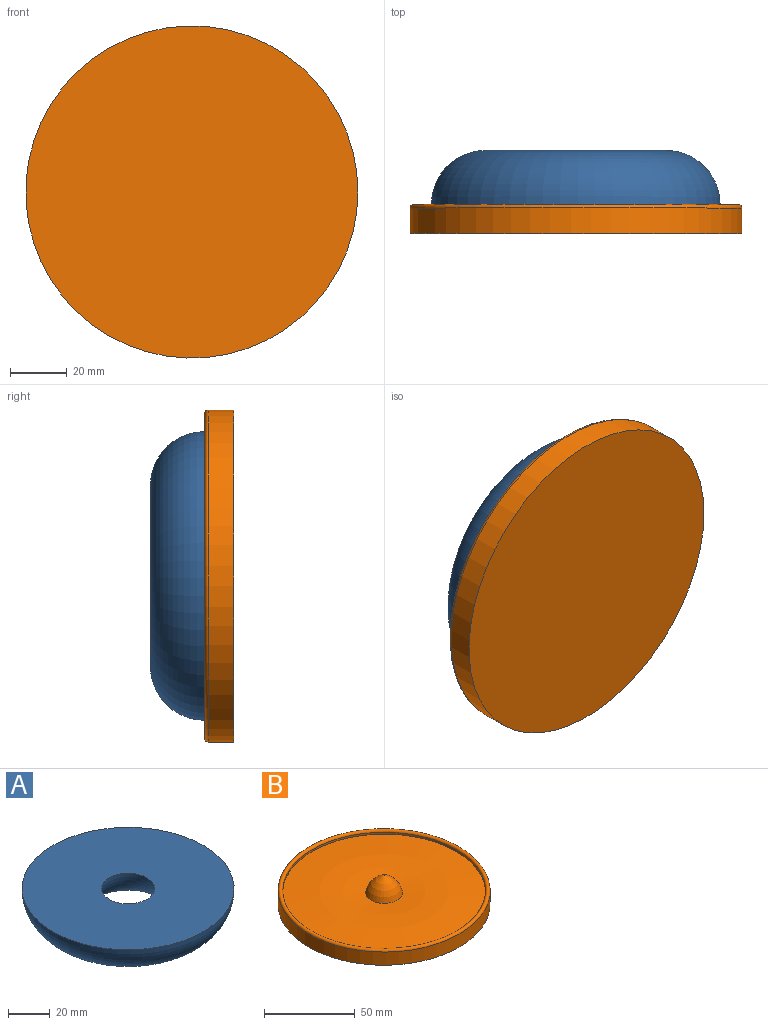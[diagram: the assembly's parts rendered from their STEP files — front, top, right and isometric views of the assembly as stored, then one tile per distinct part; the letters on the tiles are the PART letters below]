
ASSEMBLY  parts=2 mates=1
PART A: 2 faces, bbox 110x110x32.6 mm
  f0: torus R=31.75mm, axis (0,0,1), area 11939mm2, adj f1
  f1: plane 101.6x101.6mm, normal (0,0,1), area 7600.6mm2, adj f0
PART B: 6 faces, bbox 126.5x126.5x10.2 mm
  f0: cylinder r=58.42mm len=116.84mm, axis (0,0,1), area 3263.2mm2, adj f4,f5
  f1: cylinder r=55.88mm len=111.76mm, axis (0,0,1), area 445.9mm2, adj f2,f5
  f2: torus R=33.02mm, axis (0,0,1), area 9500.6mm2, adj f1,f3
  f3: revolved ~20.32x10.16mm, area 0mm2, adj f2
  f4: plane 116.84x116.84mm, normal (0,0,-1), area 10721.9mm2, adj f0
  f5: torus R=57.15mm, axis (0,0,1), area 1432.7mm2, adj f0,f1
PLACE A rot(axis=(0.92,-0.27,0.27),94.6deg) t=(0,29.07,0)mm
PLACE B rot(axis=(-1,0,0),90deg) t=(0,0,0)mm
MATE cylindrical B.f0 <-> A.f0  axis (0,-1,0) through (0,0,0)mm
